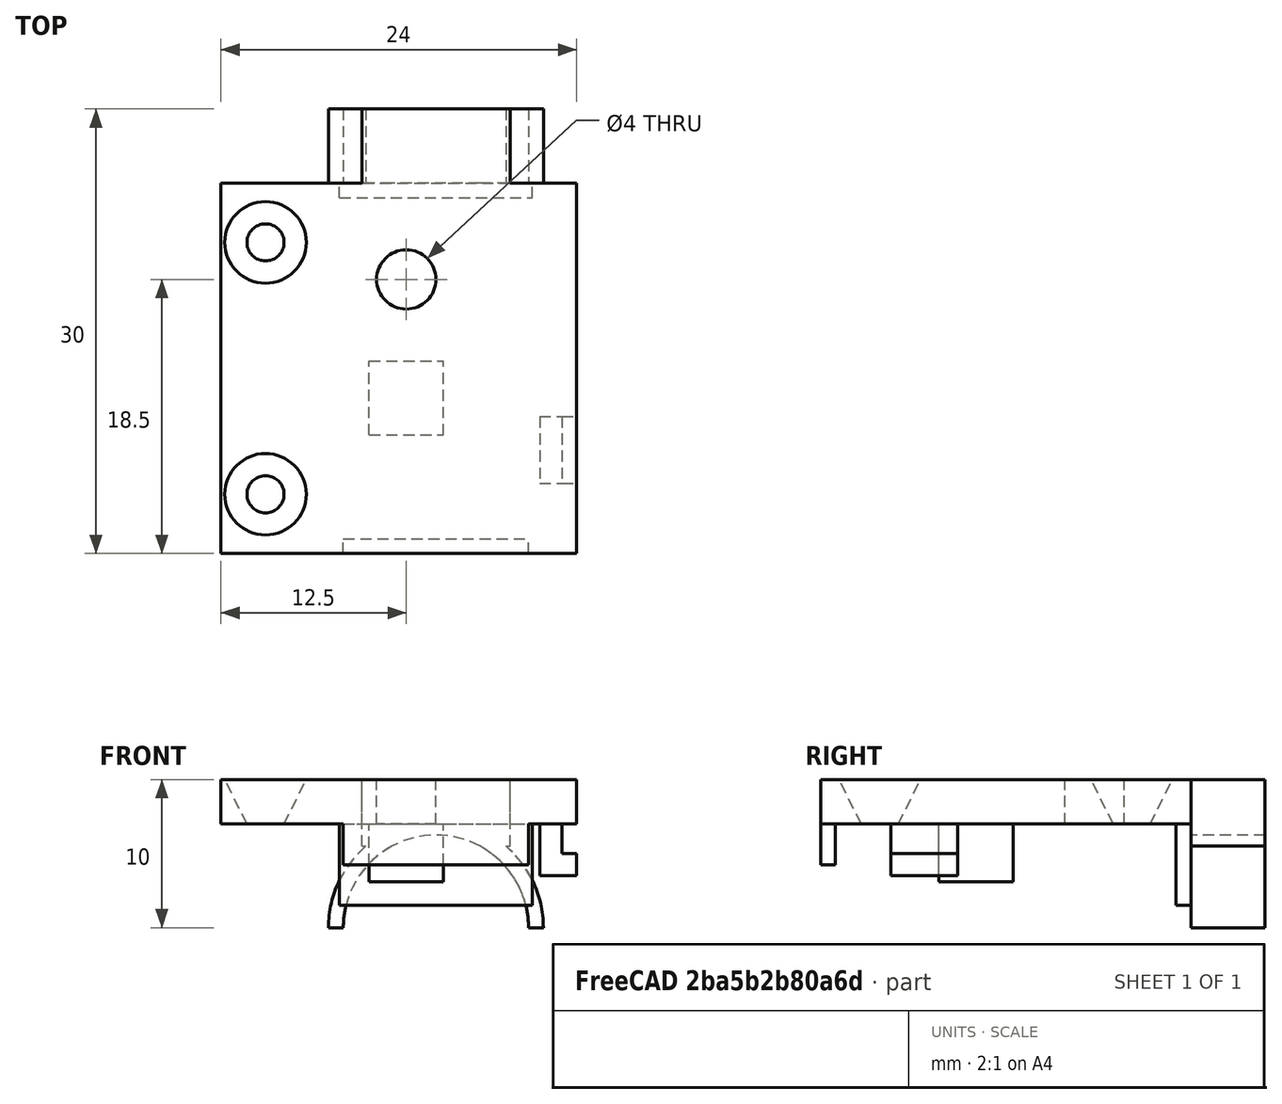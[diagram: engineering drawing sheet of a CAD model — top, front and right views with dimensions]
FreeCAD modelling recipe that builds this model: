
FCSTD DOCUMENT  (FreeCAD 0.18R16131 (Git))
Label: glowstick_case_lid
License: All rights reserved
LicenseURL: http://en.wikipedia.org/wiki/All_rights_reserved
objects: Part::Box×8, Part::MultiFuse×7, Part::Cut×6, Part::Cylinder×4, Part::Cone×2
note: 27 computed .brp shape members not serialized (recipe doc carries the construction recipe); baked Part::Feature solids carry a one-line shape summary decoded from their .brp

FEATURE [Part::Box] Box  label="Cube"
  AttacherType = Attacher::AttachEngine3D
  Height = 3
  Length = 24
  Width = 25
FEATURE [Part::Cone] Cone
  Angle = 360
  AttacherType = Attacher::AttachEngine3D
  Height = 3
  Placement = pos=(3,4,0) rot=(0,0,1;0rad)
  Radius1 = 1.25
  Radius2 = 2.75
FEATURE [Part::Cone] Cone001
  Angle = 360
  AttacherType = Attacher::AttachEngine3D
  Height = 3
  Placement = pos=(3,21,0) rot=(0,0,1;0rad)
  Radius1 = 1.25
  Radius2 = 2.75
FEATURE [Part::Box] Box001  label="Cube001"
  AttacherType = Attacher::AttachEngine3D
  Height = 5
  Length = 1.5
  Placement = pos=(21.5,4.75,-3.5) rot=(0,0,1;0rad)
  Width = 4.5
FEATURE [Part::Box] Box002  label="Cube002"
  AttacherType = Attacher::AttachEngine3D
  Height = 1.5
  Length = 2.5
  Placement = pos=(21.5,4.75,-3.5) rot=(0,0,1;0rad)
  Width = 4.5
FEATURE [Part::Cut] Cut
  Base = -> Box
  Tool = -> Cone
FEATURE [Part::Cut] Cut001
  Base = -> Cut
  Tool = -> Cone001
FEATURE [Part::MultiFuse] Fusion
  Shapes = -> [Box002,Box001]
FEATURE [Part::MultiFuse] Fusion001
  Shapes = -> [Fusion,Cut001]
FEATURE [Part::Cylinder] Cylinder
  Angle = 360
  AttacherType = Attacher::AttachEngine3D
  Height = 5
  Placement = pos=(14.5,30,-4.5) rot=(1,0,0;1.5708rad)
  Radius = 7.25
FEATURE [Part::Cylinder] Cylinder001
  Angle = 360
  AttacherType = Attacher::AttachEngine3D
  Height = 5
  Placement = pos=(14.5,30,-4.5) rot=(1,0,0;1.5708rad)
  Radius = 6.25
FEATURE [Part::Cut] Cut002
  Base = -> Cylinder
  Placement = pos=(0,0,-2.5) rot=(0,0,1;0rad)
  Tool = -> Cylinder001
FEATURE [Part::Box] Box003  label="Cube003"
  AttacherType = Attacher::AttachEngine3D
  Height = 10
  Length = 20
  Placement = pos=(5,25,-17) rot=(0,0,1;0rad)
  Width = 10
FEATURE [Part::Cut] Cut003
  Base = -> Cut002
  Tool = -> Box003
FEATURE [Part::Box] Box004  label="Cube004"
  AttacherType = Attacher::AttachEngine3D
  Height = 4.5
  Length = 10
  Placement = pos=(9.5,25,-1.5) rot=(0,0,1;0rad)
  Width = 5
FEATURE [Part::Cylinder] Cylinder002
  Angle = 360
  AttacherType = Attacher::AttachEngine3D
  Height = 10
  Placement = pos=(14.5,30,-7) rot=(1,0,0;1.5708rad)
  Radius = 6.25
FEATURE [Part::Cut] Cut004
  Base = -> Box004
  Tool = -> Cylinder002
FEATURE [Part::MultiFuse] Fusion002
  Shapes = -> [Cut003,Cut004]
FEATURE [Part::MultiFuse] Fusion003
  Shapes = -> [Fusion001,Fusion002]
FEATURE [Part::Box] Box005  label="Cube005"
  AttacherType = Attacher::AttachEngine3D
  Height = 5.5
  Length = 13
  Placement = pos=(8,24,-5.5) rot=(0,0,1;0rad)
  Width = 1
FEATURE [Part::Cylinder] Cylinder003
  Angle = 360
  AttacherType = Attacher::AttachEngine3D
  Height = 10
  Placement = pos=(12.5,18.5,0) rot=(0,0,1;0rad)
  Radius = 2
FEATURE [Part::MultiFuse] Fusion004
  Shapes = -> [Box005,Fusion003]
FEATURE [Part::Cut] Cut005
  Base = -> Fusion004
  Tool = -> Cylinder003
FEATURE [Part::Box] Box006  label="Cube006"
  AttacherType = Attacher::AttachEngine3D
  Height = 3.9
  Length = 5
  Placement = pos=(10,8,-3.9) rot=(0,0,1;0rad)
  Width = 5
FEATURE [Part::MultiFuse] Fusion005
  Shapes = -> [Cut005,Box006]
FEATURE [Part::Box] Box007  label="Cube007"
  AttacherType = Attacher::AttachEngine3D
  Height = 2.75
  Length = 12.5
  Placement = pos=(8.25,0,-2.75) rot=(0,0,1;0rad)
  Width = 1
FEATURE [Part::MultiFuse] Fusion006
  Shapes = -> [Box007,Fusion005]
